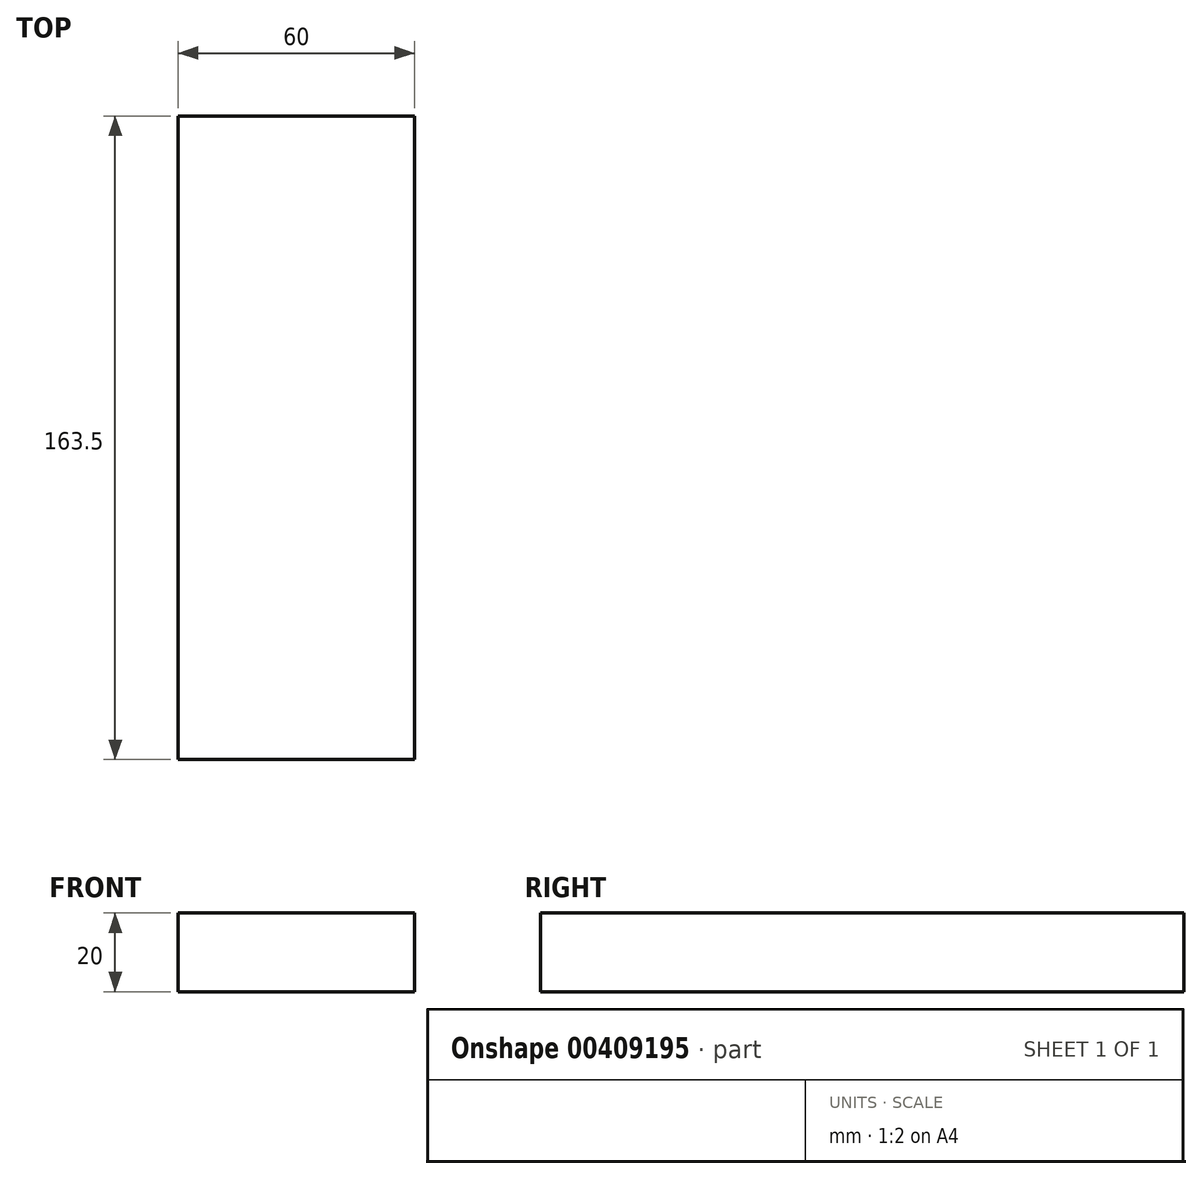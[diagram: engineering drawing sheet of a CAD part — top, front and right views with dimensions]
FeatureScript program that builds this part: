
annotation { "Feature Type Name" : "Feature", "Feature Type Description" : "" }
export const myFeature = defineFeature(function(context is Context, id is Id, definition is map)
    precondition{}
    {
        {
            var Q0;
            Q0=qCreatedBy(makeId("Top.planeOp"),FACE);
            var sketch = newSketch(context, id + "F0", { "sketchPlane" : qUnion([Q0])});
            skLineSegment(sketch, "E0", {"start": v(-30, 17.32) * mm, "end": v(30, 17.32) * mm});
            skLineSegment(sketch, "E1", {"start": v(30, 17.32) * mm, "end": v(0, -34.64) * mm, "construction": true});
            skLineSegment(sketch, "E2", {"start": v(0, -34.64) * mm, "end": v(-30, 17.32) * mm, "construction": true});
            skCircle(sketch, "E3", {"center": v(0, 0) * mm, "radius": 34.64 * mm, "construction": true});
            skLineSegment(sketch, "E4.bottom", {"start": v(-30, 180.82) * mm, "end": v(30, 180.82) * mm});
            skLineSegment(sketch, "E4.left", {"start": v(-30, 180.82) * mm, "end": v(-30, 17.32) * mm});
            skLineSegment(sketch, "E4.right", {"start": v(30, 180.82) * mm, "end": v(30, 17.32) * mm});
            skPoint(sketch, "E4.middle", {"position": v(0, 99.07) * mm});
            skLineSegment(sketch, "E5.bottom", {"start": v(-30, 180.82) * mm, "end": v(30, 180.82) * mm, "construction": true});
            skLineSegment(sketch, "E5.top", {"start": v(-30, 200.82) * mm, "end": v(30, 200.82) * mm, "construction": true});
            skLineSegment(sketch, "E5.left", {"start": v(-30, 180.82) * mm, "end": v(-30, 200.82) * mm, "construction": true});
            skLineSegment(sketch, "E5.right", {"start": v(30, 180.82) * mm, "end": v(30, 200.82) * mm, "construction": true});
            skPoint(sketch, "E5.middle", {"position": v(0, 190.82) * mm});
            skCircle(sketch, "E6", {"center": v(0, 0) * mm, "radius": 183.3 * mm, "construction": true});
            skLineSegment(sketch, "E7", {"start": v(-30, 167.32) * mm, "end": v(30, 167.32) * mm, "construction": true});
            skCircle(sketch, "E8", {"center": v(0, 0) * mm, "radius": 100 * mm, "construction": true});
            skLineSegment(sketch, "E9", {"start": v(-30, 17.32) * mm, "end": v(-171.6, -64.43) * mm, "construction": true});
            skLineSegment(sketch, "E10", {"start": v(-171.6, -64.43) * mm, "end": v(-141.6, -116.4) * mm, "construction": true});
            skLineSegment(sketch, "E11", {"start": v(-141.6, -116.4) * mm, "end": v(0, -34.64) * mm, "construction": true});
            skLineSegment(sketch, "E12", {"start": v(0, -34.64) * mm, "end": v(141.6, -116.4) * mm, "construction": true});
            skLineSegment(sketch, "E13", {"start": v(141.6, -116.4) * mm, "end": v(171.6, -64.43) * mm, "construction": true});
            skLineSegment(sketch, "E14", {"start": v(171.6, -64.43) * mm, "end": v(30, 17.32) * mm, "construction": true});
            skLineSegment(sketch, "E15", {"start": v(-30, 180.82) * mm, "end": v(-171.6, -64.43) * mm, "construction": true});
            skLineSegment(sketch, "E16", {"start": v(-141.6, -116.4) * mm, "end": v(141.6, -116.4) * mm, "construction": true});
            skLineSegment(sketch, "E17", {"start": v(171.6, -64.43) * mm, "end": v(30, 180.82) * mm, "construction": true});
            skLineSegment(sketch, "E18.bottom", {"start": v(-191.42, 200.82) * mm, "end": v(191.42, 200.82) * mm, "construction": true});
            skLineSegment(sketch, "E19", {"start": v(141.6, -116.4) * mm, "end": v(158.92, -126.4) * mm, "construction": true});
            skLineSegment(sketch, "E20", {"start": v(158.92, -126.4) * mm, "end": v(188.92, -74.43) * mm, "construction": true});
            skLineSegment(sketch, "E21", {"start": v(188.92, -74.43) * mm, "end": v(171.6, -64.43) * mm, "construction": true});
            skLineSegment(sketch, "E22", {"start": v(-188.92, -74.43) * mm, "end": v(-158.92, -126.4) * mm, "construction": true});
            skLineSegment(sketch, "E23", {"start": v(-158.92, -126.4) * mm, "end": v(-141.6, -116.4) * mm, "construction": true});
            skLineSegment(sketch, "E24", {"start": v(-188.92, -74.43) * mm, "end": v(-171.6, -64.43) * mm, "construction": true});
            skLineSegment(sketch, "E25", {"start": v(0, 180.82) * mm, "end": v(-156.6, -90.41) * mm, "construction": true});
            skLineSegment(sketch, "E26", {"start": v(-156.6, -90.41) * mm, "end": v(156.6, -90.41) * mm, "construction": true});
            skLineSegment(sketch, "E27", {"start": v(156.6, -90.41) * mm, "end": v(0, 180.82) * mm, "construction": true});
            skCircle(sketch, "E28", {"center": v(0, 100) * mm, "radius": 27 * mm, "construction": true});
            skLineSegment(sketch, "E29", {"start": v(-54, 169.84) * mm, "end": v(-54, 112.13) * mm, "construction": true});
            skLineSegment(sketch, "E30", {"start": v(-68.75, 140.82) * mm, "end": v(-11.19, 140.82) * mm, "construction": true});
            skLineSegment(sketch, "E31", {"start": v(-158.92, -126.4) * mm, "end": v(-156.42, -130.72) * mm});
            skLineSegment(sketch, "E32", {"start": v(-156.42, -130.72) * mm, "end": v(-104.45, -100.72) * mm});
            skLineSegment(sketch, "E33", {"start": v(-104.45, -100.72) * mm, "end": v(-106.95, -96.4) * mm});
            skLineSegment(sketch, "E34", {"start": v(-191.42, -130.72) * mm, "end": v(191.42, -130.72) * mm, "construction": true});
            skLineSegment(sketch, "E35", {"start": v(-173.92, -100.41) * mm, "end": v(0, 0) * mm, "construction": true});
            skLineSegment(sketch, "E36.MirrorCS", {"start": v(-139.45, -40.1) * mm, "end": v(-136.95, -44.43) * mm});
            skLineSegment(sketch, "E37.MirrorCS", {"start": v(-188.92, -74.43) * mm, "end": v(-191.42, -70.1) * mm});
            skLineSegment(sketch, "E38.MirrorCS", {"start": v(-191.42, -70.1) * mm, "end": v(-139.45, -40.1) * mm});
            skLineSegment(sketch, "E39", {"start": v(-191.42, 200.82) * mm, "end": v(-191.42, -130.72) * mm, "construction": true});
            skLineSegment(sketch, "E40.MirrorCS", {"start": v(191.42, 200.82) * mm, "end": v(191.42, -130.72) * mm, "construction": true});
            skPoint(sketch, "E41", {"position": v(-165.26, -95.41) * mm});
            skLineSegment(sketch, "E42", {"start": v(0, 180.82) * mm, "end": v(0, 0) * mm, "construction": true});
            skPoint(sketch, "E43", {"position": v(0, 174.07) * mm});
            skPoint(sketch, "E44", {"position": v(0, 167.32) * mm});
            skPoint(sketch, "E45.MirrorP", {"position": v(165.26, -95.41) * mm});
            skSolve(sketch);
        }
        {
            var Q0;
            Q0=makeQuery(id+"F0.imprint","IMPRINT",FACE,{"disambiguationData":[TD([[makeQuery(id+"F0.imprint","IMPRINT",EDGE,{"derivedFrom":sQuery(id+"F0.wireOp",EDGE,"E4.bottom")}),-1.0]])]});
            extrude(context, id + "F1", {"entities" : qUnion([Q0]), "depth" : 20 * mm});
        }
    });
